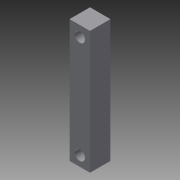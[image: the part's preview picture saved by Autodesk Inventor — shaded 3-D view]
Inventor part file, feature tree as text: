
AUTODESK INVENTOR PART (.ipt)
format: ipt  version: 2014 SP1 (Build 180222100, 222)  size: 84,992 bytes
history: native  units: in
note: dims shown in document units (in); Inventor stores cm internally (conversion verified against a paired STEP export)
features: sketch x2, extrude x1, hole x1
ambient origin geometry x8: Origin, YZ Plane, XZ Plane, XY Plane, X Axis, Y Axis, Z Axis, Center Point
bodies: Solid1 (feature_tree)
feature tree (4):
  extrude  "Extrusion1"  Depth=3.0in
  hole  "Hole1"  [1 undecoded]
  sketch  "Sketch1"  dims[d0=0.5in d1=3.0in]
  sketch  "Sketch2"  dims[d2=0.5in d3=0.0in d4=0.25in d5=0.25in d6=0.25in d7=0.75in d8=0.375in d9=0.25in d10=0.5635in d11=1.0in d12=0.8108in]
note: 1 required parameter value undecoded (feature->parameter linkage not recoverable at this tier; creation-order binding heuristic only, values carry confidence <= 0.55)
